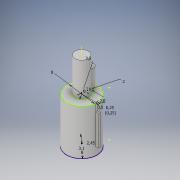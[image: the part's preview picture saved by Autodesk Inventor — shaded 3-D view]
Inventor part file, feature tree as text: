
AUTODESK INVENTOR PART (.ipt)
format: ipt  version: 2019 (Build 230136000, 136)  size: 154,112 bytes
history: native  units: in
note: dims shown in document units (in); Inventor stores cm internally (conversion verified against a paired STEP export)
features: extrude x7, sketch x4, other x1
ambient origin geometry x8: Origin, YZ Plane, XZ Plane, XY Plane, X Axis, Y Axis, Z Axis, Center Point
bodies: Solid1 (feature_tree)
feature tree (12):
  sketch  "Sketch1"  dims[d0=0.315in d1=0.0787in]
  extrude  "Extrusion1"  Depth=0.0787in
  extrude  "Extrusion2"  TaperAngle=0.0deg  [1 undecoded]
  extrude  "Extrusion3"  TaperAngle=0.0deg  [1 undecoded]
  sketch  "Sketch2"  dims[d3=0.1378in d4=0.0in]
  extrude  "Extrusion4"  Depth=0.2126in TaperAngle=0.0deg
  extrude  "Extrusion5"  Depth=0.3543in TaperAngle=0.0deg
  other  "Work Axis1"
  extrude  "Extrusion6"  Depth=0.4724in TaperAngle=0.0deg
  extrude  "Extrusion7"  Depth=0.315in
  sketch  "Sketch3"  dims[d5=0.0in d6=0.0in]
  sketch  "Sketch4"  dims[d7=0.1181in d8=0.0in d9=0.2126in d10=0.0in d11=0.3543in d12=0.0in d13=0.4724in d14=0.0in d17=0.0866in d18=0.315in d19=0.122in d20=0.0965in d21=0.3543in d22=0.0in d23=0.2441in d24=0.0in d25=0.0197in d26=0.0098in d27=0.0098in d28=0.3937in d29=0.0in d30=0.0394in d31=0.0787in d32=0.0in]
note: 2 required parameter values undecoded (feature->parameter linkage not recoverable at this tier; creation-order binding heuristic only, values carry confidence <= 0.55)
